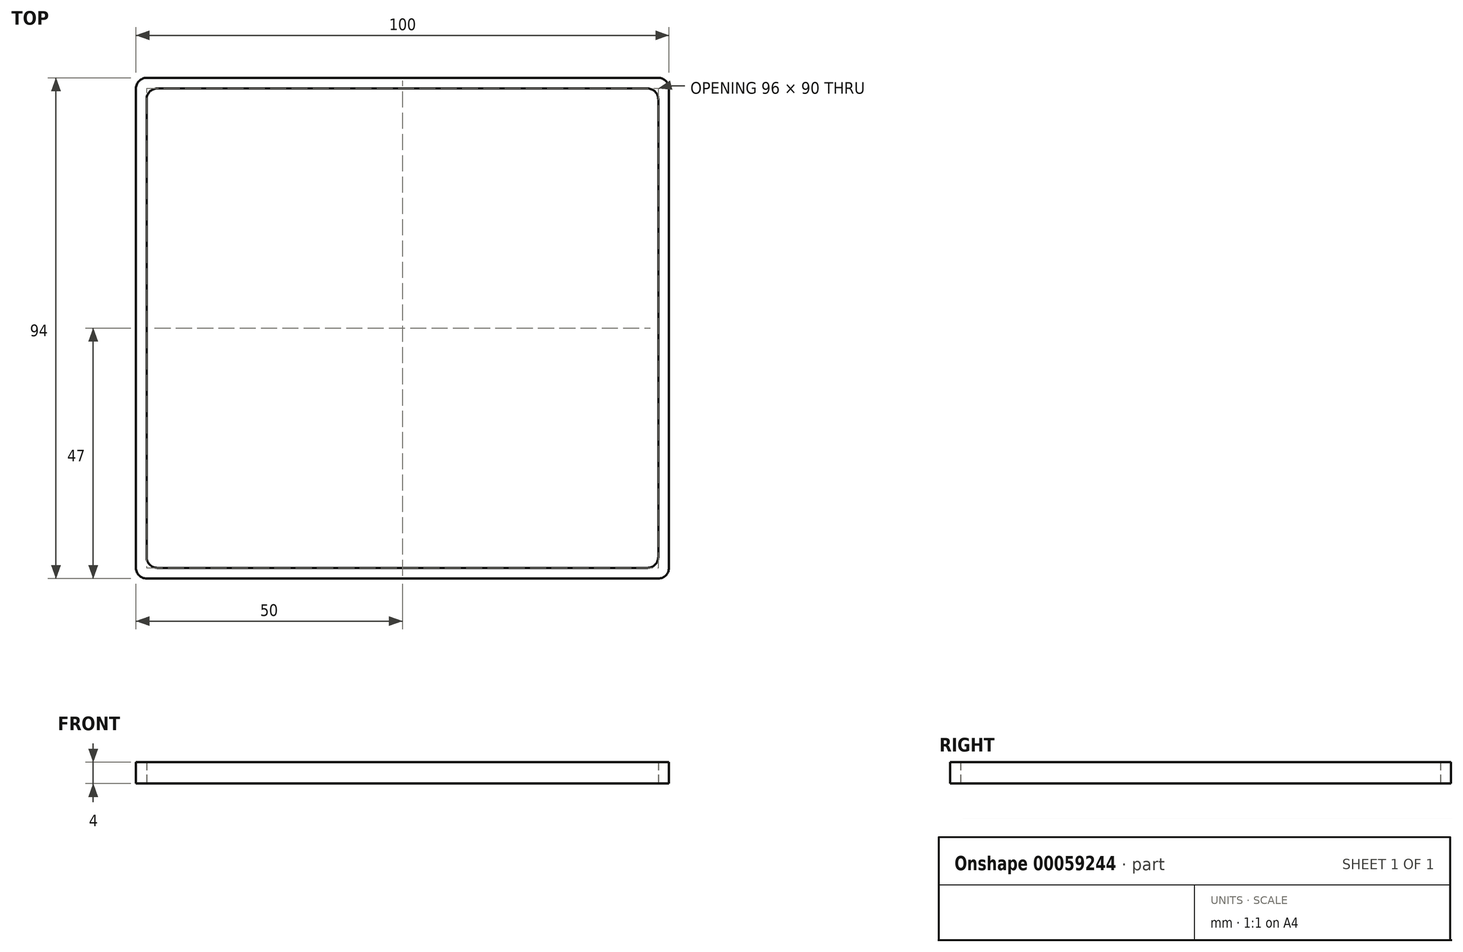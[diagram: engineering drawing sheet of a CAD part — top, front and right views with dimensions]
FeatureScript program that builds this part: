
annotation { "Feature Type Name" : "Feature", "Feature Type Description" : "" }
export const myFeature = defineFeature(function(context is Context, id is Id, definition is map)
    precondition{}
    {
        {
            var Q0;
            Q0=qCreatedBy(makeId("Top.planeOp"),FACE);
            var sketch = newSketch(context, id + "F0", { "sketchPlane" : qUnion([Q0])});
            skLineSegment(sketch, "E0.bottom", {"start": v(0, 0) * mm, "end": v(100, 0) * mm});
            skLineSegment(sketch, "E0.top", {"start": v(0, 94) * mm, "end": v(100, 94) * mm});
            skLineSegment(sketch, "E0.left", {"start": v(0, 0) * mm, "end": v(0, 94) * mm});
            skLineSegment(sketch, "E0.right", {"start": v(100, 0) * mm, "end": v(100, 94) * mm});
            skSolve(sketch);
        }
        {
            var Q0;
            Q0 = qSketchRegion(id + "F0", true);
            extrude(context, id + "F1", {"entities" : qUnion([Q0]), "depth" : 4 * mm});
        }
        {
            var Q0;
            Q0=makeQuery(id+"F1.opExtrude","CAP_FACE",FACE,{"disambiguationData":[OSD([sQuery(id+"F0.wireOp",EDGE,"E0.bottom"),sQuery(id+"F0.wireOp",EDGE,"E0.top"),sQuery(id+"F0.wireOp",EDGE,"E0.left"),sQuery(id+"F0.wireOp",EDGE,"E0.right")])],"isStart":false});
            var Q1;
            Q1=makeQuery(id+"F1.opExtrude","CAP_FACE",FACE,{"disambiguationData":[OSD([sQuery(id+"F0.wireOp",EDGE,"E0.bottom"),sQuery(id+"F0.wireOp",EDGE,"E0.top"),sQuery(id+"F0.wireOp",EDGE,"E0.left"),sQuery(id+"F0.wireOp",EDGE,"E0.right")])],"isStart":true});
            shell(context, id + "F2", {"entities" : qUnion([Q0, Q1]), "thickness" : 2 * mm});
        }
        {
            var Q0;
            Q0=makeQuery(id+"F1.opExtrude","SWEPT_EDGE",EDGE,{"disambiguationData":[OSD([sQuery(id+"F0.wireOp",EDGE,"E0.top"),sQuery(id+"F0.wireOp",EDGE,"E0.left")])]});
            var Q1;
            Q1=makeQuery(id+"F1.opExtrude","SWEPT_EDGE",EDGE,{"disambiguationData":[OSD([sQuery(id+"F0.wireOp",EDGE,"E0.bottom"),sQuery(id+"F0.wireOp",EDGE,"E0.left")])]});
            var Q2;
            Q2=makeQuery(id+"F1.opExtrude","SWEPT_EDGE",EDGE,{"disambiguationData":[OSD([sQuery(id+"F0.wireOp",EDGE,"E0.top"),sQuery(id+"F0.wireOp",EDGE,"E0.right")])]});
            var Q3;
            Q3=makeQuery(id+"F1.opExtrude","SWEPT_EDGE",EDGE,{"disambiguationData":[OSD([sQuery(id+"F0.wireOp",EDGE,"E0.bottom"),sQuery(id+"F0.wireOp",EDGE,"E0.right")])]});
            var Q4;
            Q4=makeQuery(id+"F2.opShell","OFFSET_EDGE",EDGE,{"disambiguationData":[OSD([sQuery(id+"F0.wireOp",EDGE,"E0.top"),sQuery(id+"F0.wireOp",EDGE,"E0.left")])]});
            var Q5;
            Q5=makeQuery(id+"F2.opShell","OFFSET_EDGE",EDGE,{"disambiguationData":[OSD([sQuery(id+"F0.wireOp",EDGE,"E0.bottom"),sQuery(id+"F0.wireOp",EDGE,"E0.left")])]});
            var Q6;
            Q6=makeQuery(id+"F2.opShell","OFFSET_EDGE",EDGE,{"disambiguationData":[OSD([sQuery(id+"F0.wireOp",EDGE,"E0.top"),sQuery(id+"F0.wireOp",EDGE,"E0.right")])]});
            var Q7;
            Q7=makeQuery(id+"F2.opShell","OFFSET_EDGE",EDGE,{"disambiguationData":[OSD([sQuery(id+"F0.wireOp",EDGE,"E0.bottom"),sQuery(id+"F0.wireOp",EDGE,"E0.right")])]});
            fillet(context, id + "F3", {"entities" : qUnion([Q0, Q1, Q2, Q3, Q4, Q5, Q6, Q7]), "radius" : 2 * mm, "tangentPropagation" : true, "allowEdgeOverflow" : false});
        }
    });
